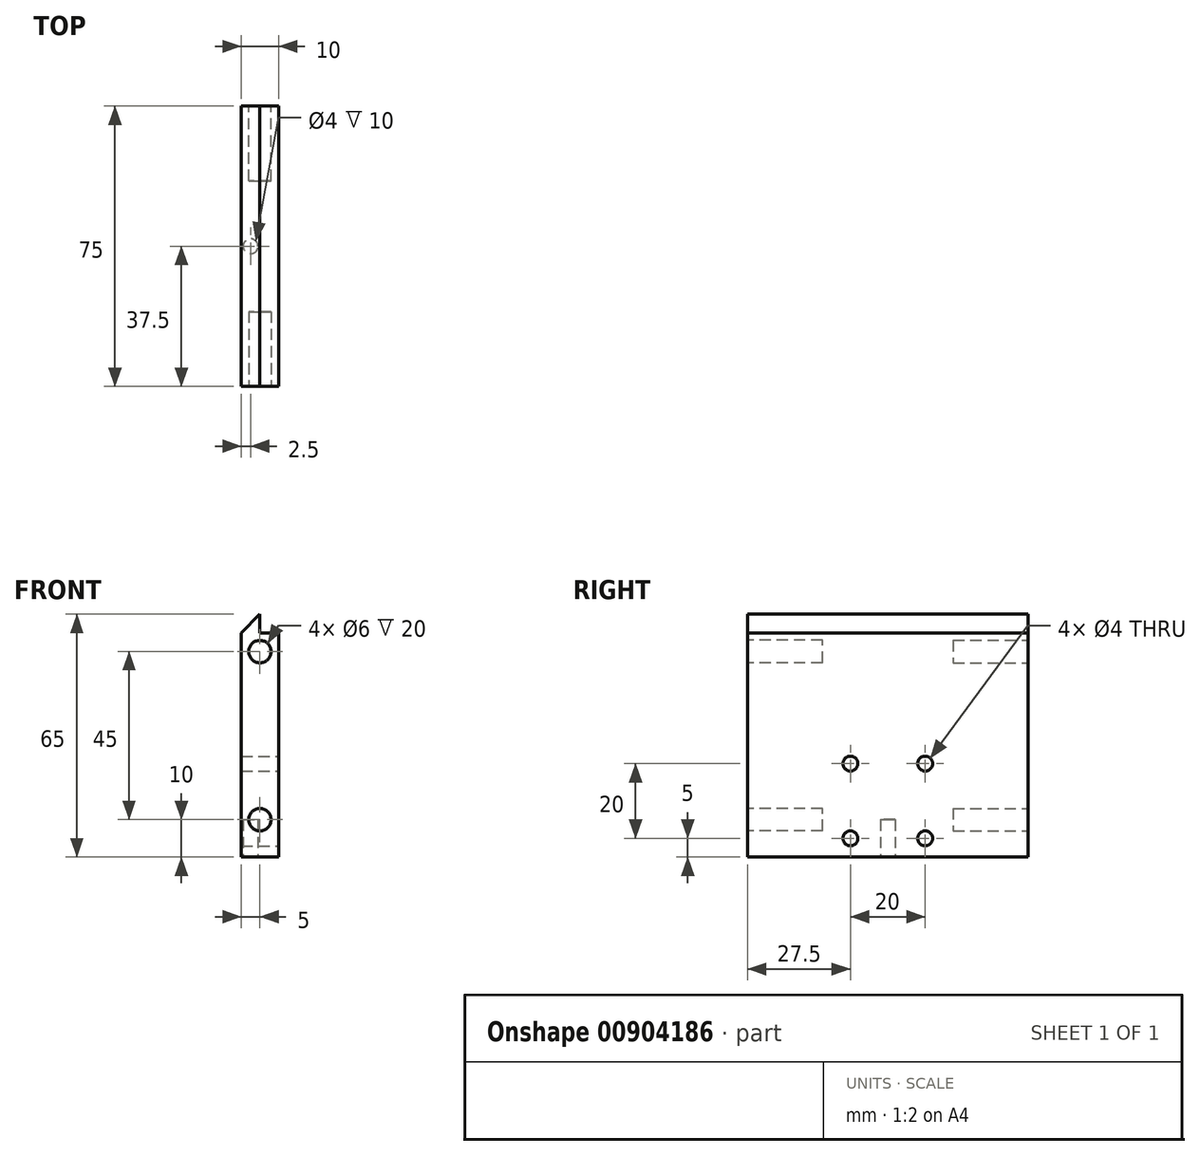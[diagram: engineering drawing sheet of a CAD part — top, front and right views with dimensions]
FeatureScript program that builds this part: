
annotation { "Feature Type Name" : "Feature", "Feature Type Description" : "" }
export const myFeature = defineFeature(function(context is Context, id is Id, definition is map)
    precondition{}
    {
        {
            var Q0;
            Q0=qCreatedBy(makeId("Front.planeOp"),FACE);
            var sketch = newSketch(context, id + "F0", { "sketchPlane" : qUnion([Q0])});
            skLineSegment(sketch, "E0.top", {"start": v(-5, -32.5) * mm, "end": v(5, -32.5) * mm});
            skLineSegment(sketch, "E0.left", {"start": v(-5, 27.5) * mm, "end": v(-5, -32.5) * mm});
            skLineSegment(sketch, "E0.right", {"start": v(5, 27.5) * mm, "end": v(5, -32.5) * mm});
            skPoint(sketch, "E0.middle", {"position": v(0, 0) * mm});
            skPoint(sketch, "E1", {"position": v(0, -22.5) * mm});
            skPoint(sketch, "E2", {"position": v(0, 22.5) * mm});
            skLineSegment(sketch, "E3", {"start": v(0, 32.5) * mm, "end": v(-5, 27.5) * mm});
            skLineSegment(sketch, "E4.top", {"start": v(0, 27.5) * mm, "end": v(5, 27.5) * mm});
            skLineSegment(sketch, "E4.left", {"start": v(0, 32.5) * mm, "end": v(0, 27.5) * mm});
            skSolve(sketch);
        }
        {
            var Q0;
            {var subQ1=sQuery(id+"F0.wireOp",EDGE,"E0.top");Q0=makeQuery(id+"F0.imprint","IMPRINT",FACE,{"disambiguationData":[TD([[makeQuery(id+"F0.imprint","IMPRINT",EDGE,{"derivedFrom":subQ1}),1.0]])]});}
            extrude(context, id + "F1", {"entities" : qUnion([Q0]), "depth" : 75 * mm, "offsetDistance" : 25 * mm});
        }
        {
            var Q0;
            Q0=makeQuery(id+"F1.opExtrude","SWEPT_FACE",FACE,{"disambiguationData":[OSD([sQuery(id+"F0.wireOp",EDGE,"E0.top")])]});
            var sketch = newSketch(context, id + "F2", { "sketchPlane" : qUnion([Q0])});
            skPoint(sketch, "E5.centerSnap0", {"position": v(-5, 37.5) * mm});
            skCircle(sketch, "E6", {"center": v(-2.5, 37.5) * mm, "radius": 2 * mm});
            skSolve(sketch);
        }
        {
            var Q0;
            Q0=makeQuery(id+"F1.opExtrude","SWEPT_FACE",FACE,{"disambiguationData":[OSD([sQuery(id+"F0.wireOp",EDGE,"E0.right")])]});
            var sketch = newSketch(context, id + "F3", { "sketchPlane" : qUnion([Q0])});
            skCircle(sketch, "E7", {"center": v(-47.5, -27.5) * mm, "radius": 2 * mm});
            skCircle(sketch, "E8", {"center": v(-47.5, -7.5) * mm, "radius": 2 * mm});
            skCircle(sketch, "E9", {"center": v(-27.5, -7.5) * mm, "radius": 2 * mm});
            skCircle(sketch, "E10", {"center": v(-27.5, -27.5) * mm, "radius": 2 * mm});
            skSolve(sketch);
        }
        {
            var Q0;
            Q0=qSketchRegion(id+"F3",true);
            extrude(context, id + "F4", {"entities" : qUnion([Q0]), "operationType" : NewBodyOperationType.REMOVE, "oppositeDirection" : true, "depth" : 25 * mm, "offsetDistance" : 25 * mm});
        }
        {
            var Q0;
            Q0=makeQuery(id+"F1.opExtrude","SWEPT_FACE",FACE,{"disambiguationData":[OSD([sQuery(id+"F0.wireOp",EDGE,"E0.top")])]});
            var sketch = newSketch(context, id + "F5", { "sketchPlane" : qUnion([Q0])});
            skSolve(sketch);
        }
        {
            var Q0;
            Q0=makeQuery(id+"F1.opExtrude","CAP_FACE",FACE,{"disambiguationData":[OSD([sQuery(id+"F0.wireOp",EDGE,"E0.top"),sQuery(id+"F0.wireOp",EDGE,"E0.left"),sQuery(id+"F0.wireOp",EDGE,"E0.right"),sQuery(id+"F0.wireOp",EDGE,"E3"),sQuery(id+"F0.wireOp",EDGE,"E4.top"),sQuery(id+"F0.wireOp",EDGE,"E4.left")])],"isStart":false});
            var sketch = newSketch(context, id + "F6", { "sketchPlane" : qUnion([Q0])});
            skCircle(sketch, "E11", {"center": v(0, -22.5) * mm, "radius": 3 * mm});
            skPoint(sketch, "E11.centerSnap0", {"position": v(0, -32.5) * mm});
            skSolve(sketch);
        }
        {
            var Q0;
            Q0=qSketchRegion(id+"F6",true);
            extrude(context, id + "F7", {"entities" : qUnion([Q0]), "operationType" : NewBodyOperationType.REMOVE, "oppositeDirection" : true, "depth" : 20 * mm, "offsetDistance" : 25 * mm});
        }
        {
            var Q0;
            Q0=makeQuery(id+"F1.opExtrude","CAP_FACE",FACE,{"disambiguationData":[OSD([sQuery(id+"F0.wireOp",EDGE,"E0.top"),sQuery(id+"F0.wireOp",EDGE,"E0.left"),sQuery(id+"F0.wireOp",EDGE,"E0.right"),sQuery(id+"F0.wireOp",EDGE,"E3"),sQuery(id+"F0.wireOp",EDGE,"E4.top"),sQuery(id+"F0.wireOp",EDGE,"E4.left")])],"isStart":false});
            var sketch = newSketch(context, id + "F8", { "sketchPlane" : qUnion([Q0])});
            skCircle(sketch, "E12", {"center": v(0, 22.5) * mm, "radius": 3 * mm});
            skSolve(sketch);
        }
        {
            var Q0;
            Q0=qSketchRegion(id+"F8",true);
            extrude(context, id + "F9", {"entities" : qUnion([Q0]), "operationType" : NewBodyOperationType.REMOVE, "oppositeDirection" : true, "depth" : 20 * mm, "offsetDistance" : 25 * mm});
        }
        {
            var Q0;
            Q0=makeQuery(id+"F1.opExtrude","CAP_FACE",FACE,{"disambiguationData":[OSD([sQuery(id+"F0.wireOp",EDGE,"E0.top"),sQuery(id+"F0.wireOp",EDGE,"E0.left"),sQuery(id+"F0.wireOp",EDGE,"E0.right"),sQuery(id+"F0.wireOp",EDGE,"E3"),sQuery(id+"F0.wireOp",EDGE,"E4.top"),sQuery(id+"F0.wireOp",EDGE,"E4.left")])],"isStart":true});
            var sketch = newSketch(context, id + "F10", { "sketchPlane" : qUnion([Q0])});
            skCircle(sketch, "E13", {"center": v(0, -22.5) * mm, "radius": 3 * mm});
            skPoint(sketch, "E13.centerSnap0", {"position": v(0, -32.5) * mm});
            skSolve(sketch);
        }
        {
            var Q0;
            Q0=qSketchRegion(id+"F10",true);
            extrude(context, id + "F11", {"entities" : qUnion([Q0]), "operationType" : NewBodyOperationType.REMOVE, "oppositeDirection" : true, "depth" : 20 * mm, "offsetDistance" : 25 * mm});
        }
        {
            var Q0;
            Q0=makeQuery(id+"F1.opExtrude","CAP_FACE",FACE,{"disambiguationData":[OSD([sQuery(id+"F0.wireOp",EDGE,"E0.top"),sQuery(id+"F0.wireOp",EDGE,"E0.left"),sQuery(id+"F0.wireOp",EDGE,"E0.right"),sQuery(id+"F0.wireOp",EDGE,"E3"),sQuery(id+"F0.wireOp",EDGE,"E4.top"),sQuery(id+"F0.wireOp",EDGE,"E4.left")])],"isStart":true});
            var sketch = newSketch(context, id + "F12", { "sketchPlane" : qUnion([Q0])});
            skCircle(sketch, "E14", {"center": v(0, 22.5) * mm, "radius": 3 * mm});
            skPoint(sketch, "E14.centerSnap0", {"position": v(0, -32.5) * mm});
            skSolve(sketch);
        }
        {
            var Q0;
            Q0=qSketchRegion(id+"F12",true);
            extrude(context, id + "F13", {"entities" : qUnion([Q0]), "operationType" : NewBodyOperationType.REMOVE, "oppositeDirection" : true, "depth" : 20 * mm, "offsetDistance" : 25 * mm});
        }
        {
            var Q0;
            Q0=qSketchRegion(id+"F2",true);
            extrude(context, id + "F14", {"entities" : qUnion([Q0]), "operationType" : NewBodyOperationType.REMOVE, "oppositeDirection" : true, "depth" : 10 * mm, "offsetDistance" : 25 * mm});
        }
        {
            var Q0;
            Q0=qSketchRegion(id+"F3",true);
            extrude(context, id + "F15", {"entities" : qUnion([Q0]), "operationType" : NewBodyOperationType.REMOVE, "oppositeDirection" : true, "depth" : 25 * mm, "offsetDistance" : 25 * mm});
        }
    });
